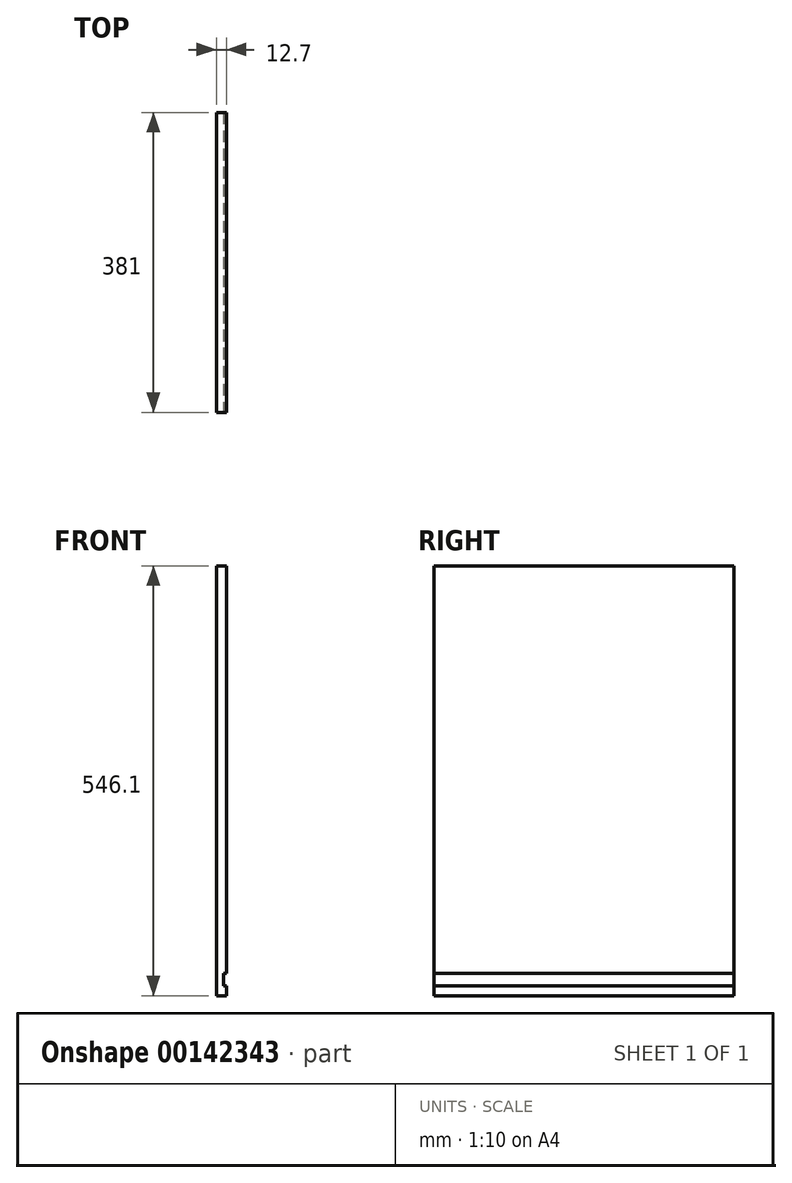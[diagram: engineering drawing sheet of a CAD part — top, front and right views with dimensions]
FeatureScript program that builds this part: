
annotation { "Feature Type Name" : "Feature", "Feature Type Description" : "" }
export const myFeature = defineFeature(function(context is Context, id is Id, definition is map)
    precondition{}
    {
        {
            var Q0;
            Q0=qCreatedBy(makeId("Right.planeOp"),FACE);
            var sketch = newSketch(context, id + "F0", { "sketchPlane" : qUnion([Q0])});
            skLineSegment(sketch, "E0.bottom", {"start": v(190.5, 330.84) * mm, "end": v(-190.5, 330.84) * mm});
            skLineSegment(sketch, "E0.top", {"start": v(190.5, -215.26) * mm, "end": v(-190.5, -215.26) * mm});
            skLineSegment(sketch, "E0.left", {"start": v(190.5, 330.84) * mm, "end": v(190.5, -215.26) * mm});
            skLineSegment(sketch, "E0.right", {"start": v(-190.5, 330.84) * mm, "end": v(-190.5, -215.26) * mm});
            skSolve(sketch);
        }
        {
            var Q0;
            Q0=makeQuery(id+"F0.imprint","IMPRINT",FACE,{"disambiguationData":[TD([[makeQuery(id+"F0.imprint","IMPRINT",EDGE,{"derivedFrom":sQuery(id+"F0.wireOp",EDGE,"E0.bottom")}),1.0]])]});
            extrude(context, id + "F1", {"entities" : qUnion([Q0]), "depth" : 12.7 * mm});
        }
        {
            var Q0;
            Q0=makeQuery(id+"F1.opExtrude","SWEPT_FACE",FACE,{"disambiguationData":[OSD([sQuery(id+"F0.wireOp",EDGE,"E0.right")])]});
            var sketch = newSketch(context, id + "F2", { "sketchPlane" : qUnion([Q0])});
            skLineSegment(sketch, "E1", {"start": v(12.7, -202.56) * mm, "end": v(9.43, -202.56) * mm});
            skLineSegment(sketch, "E2", {"start": v(9.43, -202.56) * mm, "end": v(9.43, -186.68) * mm});
            skLineSegment(sketch, "E3", {"start": v(9.43, -186.68) * mm, "end": v(12.7, -186.68) * mm});
            skSolve(sketch);
        }
        {
            var Q0;
            {var subQ0=sQuery(id+"F2.wireOp",EDGE,"E1");Q0=makeQuery(id+"F2.imprint","IMPRINT",FACE,{"disambiguationData":[TD([[makeQuery(id+"F2.imprint","IMPRINT",EDGE,{"derivedFrom":subQ0}),-1.0]])]});}
            extrude(context, id + "F3", {"entities" : qUnion([Q0]), "operationType" : NewBodyOperationType.REMOVE, "oppositeDirection" : true, "depth" : 424.43 * mm});
        }
    });
